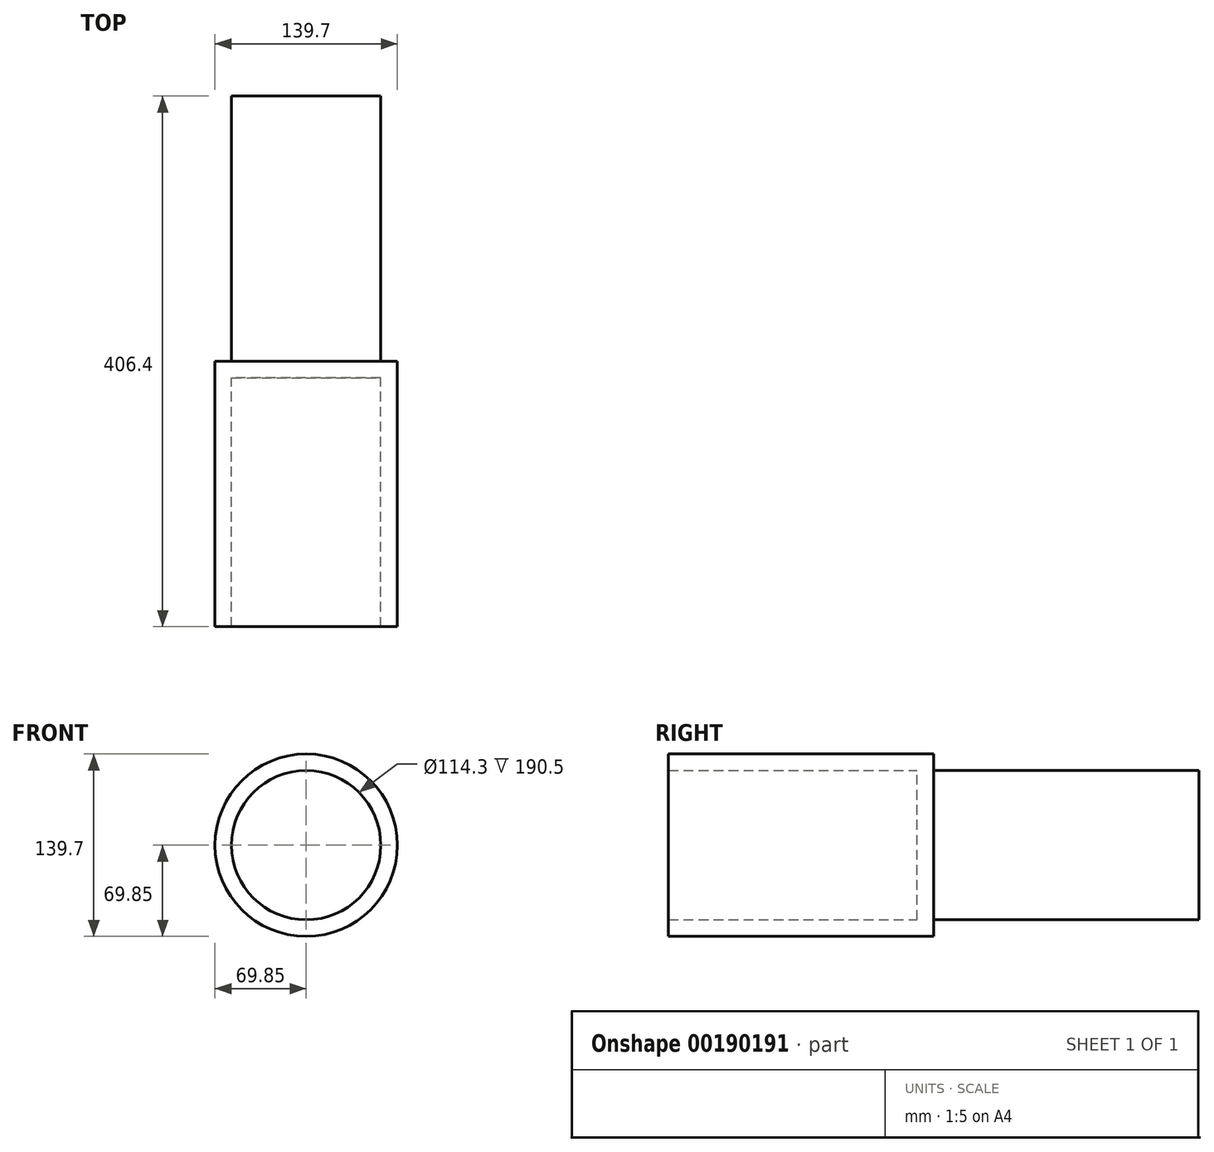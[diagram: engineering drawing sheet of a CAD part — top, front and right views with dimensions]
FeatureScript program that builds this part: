
annotation { "Feature Type Name" : "Feature", "Feature Type Description" : "" }
export const myFeature = defineFeature(function(context is Context, id is Id, definition is map)
    precondition{}
    {
        {
            var Q0;
            Q0=qCreatedBy(makeId("Front.planeOp"),FACE);
            var sketch = newSketch(context, id + "F0", { "sketchPlane" : qUnion([Q0])});
            skCircle(sketch, "E0", {"center": v(0, 0) * mm, "radius": 69.85 * mm});
            skCircle(sketch, "E1", {"center": v(0, 0) * mm, "radius": 57.15 * mm});
            skSolve(sketch);
        }
        {
            var Q0;
            Q0 = qSketchRegion(id + "F0", true);
            extrude(context, id + "F1", {"entities" : qUnion([Q0]), "depth" : 203.2 * mm});
        }
        {
            var Q0;
            Q0=qCreatedBy(makeId("Front.planeOp"),FACE);
            var sketch = newSketch(context, id + "F2", { "sketchPlane" : qUnion([Q0])});
            skCircle(sketch, "E2", {"center": v(0, 0) * mm, "radius": 57.15 * mm});
            skSolve(sketch);
        }
        {
            var Q0;
            Q0 = qSketchRegion(id + "F2", true);
            extrude(context, id + "F3", {"entities" : qUnion([Q0]), "operationType" : NewBodyOperationType.ADD, "depth" : 12.7 * mm});
        }
        {
            var Q0;
            Q0 = qSketchRegion(id + "F2", true);
            extrude(context, id + "F4", {"entities" : qUnion([Q0]), "operationType" : NewBodyOperationType.ADD, "oppositeDirection" : true, "depth" : 203.2 * mm});
        }
    });
